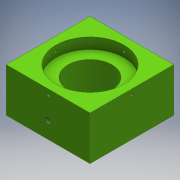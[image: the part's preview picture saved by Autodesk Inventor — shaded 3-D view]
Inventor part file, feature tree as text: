
AUTODESK INVENTOR PART (.ipt)
format: ipt  version: 2016 (Build 200138000, 138)  size: 157,184 bytes
history: native  units: mm
features: sketch x6, extrude x3, hole x3, pattern_circular x1
ambient origin geometry x8: Origin, YZ Plane, XZ Plane, XY Plane, X Axis, Y Axis, Z Axis, Center Point
bodies: Solid1 (feature_tree)
feature tree (13):
  extrude  "baseExtrusion"  Depth=76.2mm
  extrude  "tlExtrusion"  Depth=38.1mm
  extrude  "lightPathExtrusion"  Depth=40.0mm
  hole  "tubeLensGrubScrew1"  [1 undecoded]
  pattern_circular  "tubeLensGrubScrew2"  Count=2 Angle=90.0deg
  hole  "60mmCageSystem"  [1 undecoded]
  hole  "m6MountingHole"  [1 undecoded]
  sketch  "Sketch1"  dims[d0=76.2mm d1=76.2mm]
  sketch  "Sketch2"  dims[d2=38.1mm d3=38.1mm]
  sketch  "Sketch3"  dims[d4=40.0mm d5=0.0mm d6=62.0mm]
  sketch  "Sketch4"  dims[d7=10.0mm d8=0.0mm d9=40.0mm]
  sketch  "Sketch5"  dims[d10=10.0mm d11=0.0mm]
  sketch  "Sketch6"  dims[d12=5.0mm d13=2.459mm d14=6.0mm d15=4.0mm d16=2.0mm d17=90.0deg d18=9.525mm d19=20.594885mm d20=20.0mm d21=90.0deg d23=60.0mm d24=60.0mm d25=30.0mm d26=30.0mm d27=2.156mm d28=5.0mm d29=4.0mm d30=2.0mm d31=90.0deg d32=10.0mm d33=20.594885mm d34=15.0mm d35=4.917mm d36=10.0mm d37=4.0mm d38=2.0mm d39=90.0deg d40=15.0mm d41=20.594885mm]
note: 3 required parameter values undecoded (feature->parameter linkage not recoverable at this tier; creation-order binding heuristic only, values carry confidence <= 0.55)
